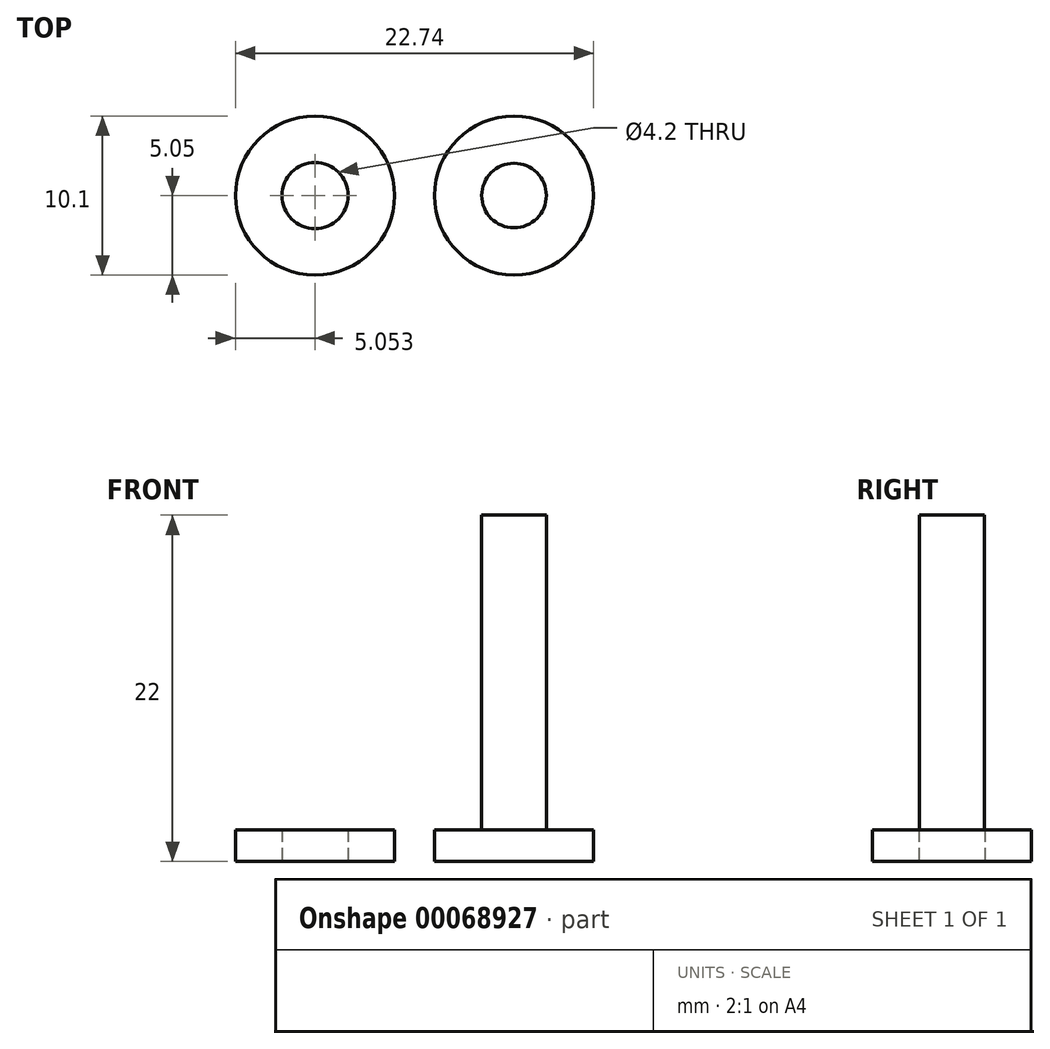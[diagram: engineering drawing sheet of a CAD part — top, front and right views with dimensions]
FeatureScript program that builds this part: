
annotation { "Feature Type Name" : "Feature", "Feature Type Description" : "" }
export const myFeature = defineFeature(function(context is Context, id is Id, definition is map)
    precondition{}
    {
        {
            var Q0;
            Q0=qCreatedBy(makeId("Top.planeOp"),FACE);
            var sketch = newSketch(context, id + "F0", { "sketchPlane" : qUnion([Q0])});
            skCircle(sketch, "E0", {"center": v(0, 0) * mm, "radius": 2.05 * mm});
            skCircle(sketch, "E1", {"center": v(0, 0) * mm, "radius": 5.05 * mm});
            skCircle(sketch, "E2", {"center": v(-12.64, 0) * mm, "radius": 2.1 * mm});
            skCircle(sketch, "E3", {"center": v(-12.64, 0) * mm, "radius": 5.05 * mm});
            skSolve(sketch);
        }
        {
            var Q0;
            Q0 = qSketchRegion(id + "F0", true);
            var Q1;
            Q1=makeQuery(id+"F0.imprint","IMPRINT",FACE,{"disambiguationData":[TD([[makeQuery(id+"F0.imprint","IMPRINT",EDGE,{"derivedFrom":sQuery(id+"F0.wireOp",EDGE,"E0")}),1.0]])]});
            extrude(context, id + "F1", {"entities" : qUnion([Q0, Q1]), "depth" : 2 * mm});
        }
        {
            var Q0;
            Q0=makeQuery(id+"F0.imprint","IMPRINT",FACE,{"disambiguationData":[TD([[makeQuery(id+"F0.imprint","IMPRINT",EDGE,{"derivedFrom":sQuery(id+"F0.wireOp",EDGE,"E0")}),1.0]])]});
            extrude(context, id + "F2", {"entities" : qUnion([Q0]), "operationType" : NewBodyOperationType.ADD, "depth" : 22 * mm});
        }
    });
